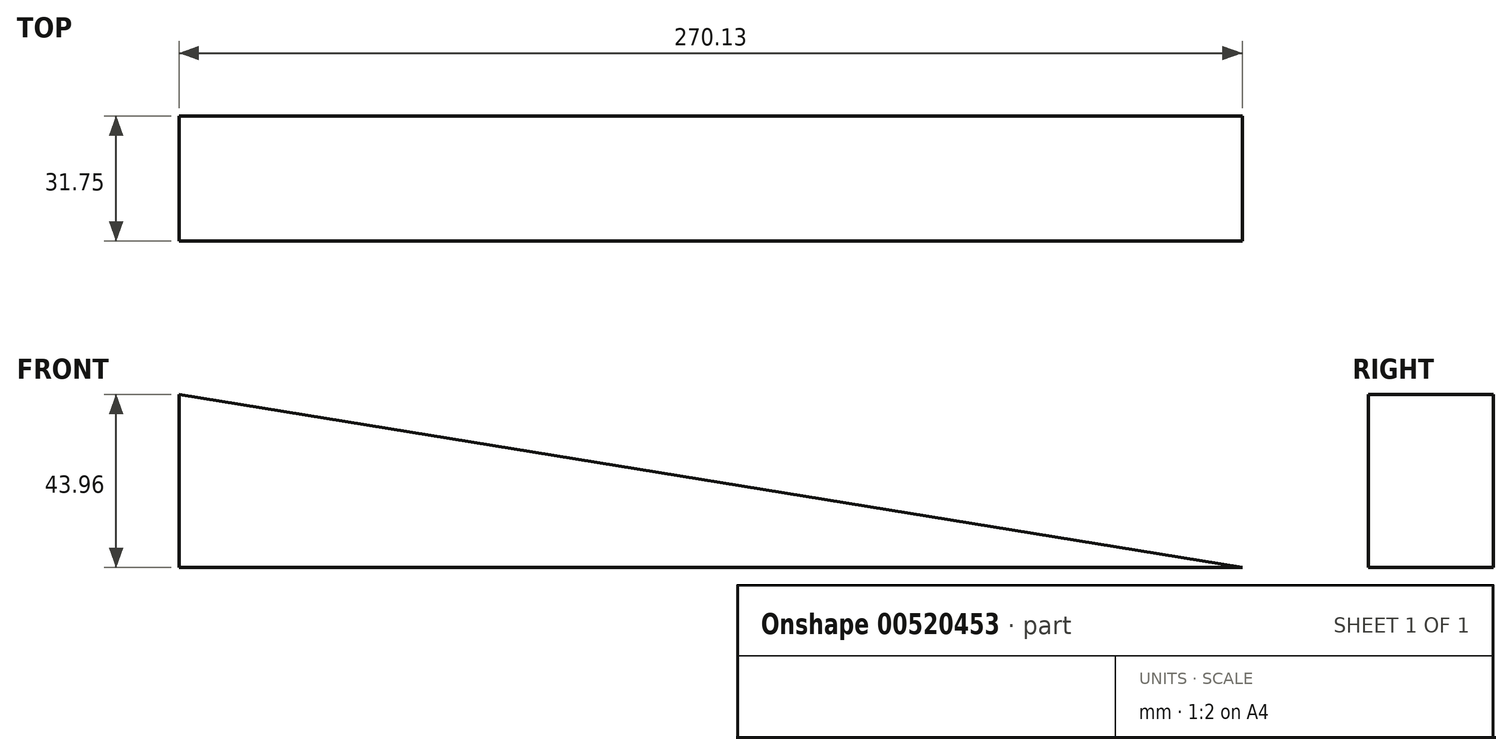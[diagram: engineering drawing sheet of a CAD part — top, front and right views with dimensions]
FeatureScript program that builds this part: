
annotation { "Feature Type Name" : "Feature", "Feature Type Description" : "" }
export const myFeature = defineFeature(function(context is Context, id is Id, definition is map)
    precondition{}
    {
        {
            var Q0;
            Q0=qCreatedBy(makeId("Front.planeOp"),FACE);
            var sketch = newSketch(context, id + "F0", { "sketchPlane" : qUnion([Q0])});
            skLineSegment(sketch, "E0", {"start": v(-212.93, 24.04) * mm, "end": v(-212.93, -19.92) * mm});
            skLineSegment(sketch, "E1", {"start": v(-212.93, -19.92) * mm, "end": v(57.2, -19.92) * mm});
            skLineSegment(sketch, "E2", {"start": v(-212.93, 24.04) * mm, "end": v(57.2, -19.92) * mm});
            skSolve(sketch);
        }
        {
            var Q0;
            Q0=makeQuery(id+"F0.imprint","IMPRINT",FACE,{"disambiguationData":[TD([[makeQuery(id+"F0.imprint","IMPRINT",EDGE,{"derivedFrom":sQuery(id+"F0.wireOp",EDGE,"E0")}),1.0]])]});
            extrude(context, id + "F1", {"entities" : qUnion([Q0]), "depth" : 31.75 * mm, "offsetDistance" : 25.4 * mm});
        }
    });
